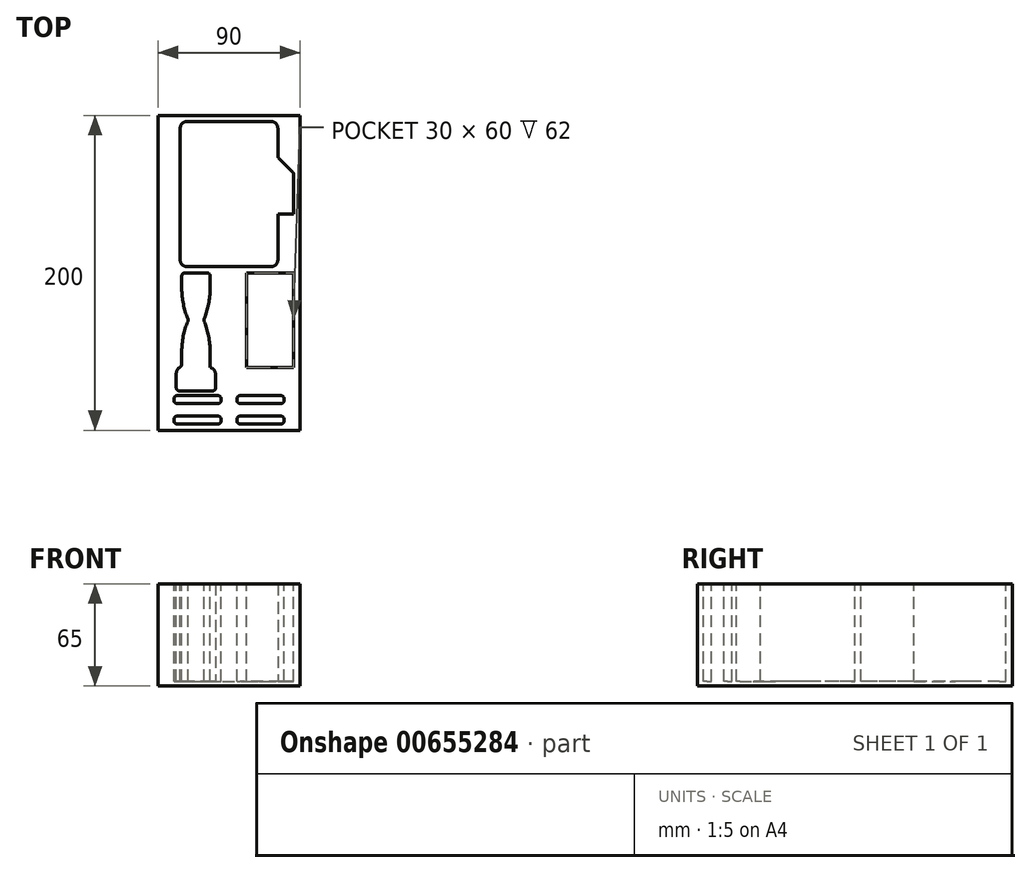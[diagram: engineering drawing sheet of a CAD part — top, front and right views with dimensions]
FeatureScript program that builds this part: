
annotation { "Feature Type Name" : "Feature", "Feature Type Description" : "" }
export const myFeature = defineFeature(function(context is Context, id is Id, definition is map)
    precondition{}
    {
        {
            var Q0;
            Q0=qCreatedBy(makeId("Top.planeOp"),FACE);
            var sketch = newSketch(context, id + "F0", { "sketchPlane" : qUnion([Q0])});
            skLineSegment(sketch, "E0.bottom", {"start": v(-45, -100) * mm, "end": v(45, -100) * mm});
            skLineSegment(sketch, "E0.top", {"start": v(-45, 100) * mm, "end": v(45, 100) * mm});
            skLineSegment(sketch, "E0.left", {"start": v(-45, -100) * mm, "end": v(-45, 100) * mm});
            skLineSegment(sketch, "E0.right", {"start": v(45, -100) * mm, "end": v(45, 100) * mm});
            skSolve(sketch);
        }
        {
            var Q0;
            Q0=makeQuery(id+"F0.imprint","IMPRINT",FACE,{"disambiguationData":[TD([[makeQuery(id+"F0.imprint","IMPRINT",EDGE,{"derivedFrom":sQuery(id+"F0.wireOp",EDGE,"E0.bottom")}),1.0]])]});
            extrude(context, id + "F1", {"entities" : qUnion([Q0]), "depth" : 65 * mm, "offsetDistance" : 25 * mm});
        }
        {
            var Q0;
            Q0=makeQuery(id+"F1.opExtrude","CAP_FACE",FACE,{"disambiguationData":[OSD([sQuery(id+"F0.wireOp",EDGE,"E0.bottom"),sQuery(id+"F0.wireOp",EDGE,"E0.top"),sQuery(id+"F0.wireOp",EDGE,"E0.left"),sQuery(id+"F0.wireOp",EDGE,"E0.right")])],"isStart":false});
            var sketch = newSketch(context, id + "F2", { "sketchPlane" : qUnion([Q0])});
            skLineSegment(sketch, "E1.bottom", {"start": v(-31, 96) * mm, "end": v(31, 96) * mm});
            skLineSegment(sketch, "E1.top", {"start": v(-31, 4) * mm, "end": v(31, 4) * mm});
            skLineSegment(sketch, "E1.left", {"start": v(-31, 96) * mm, "end": v(-31, 4) * mm});
            skLineSegment(sketch, "E1.right", {"start": v(31, 96) * mm, "end": v(31, 4) * mm});
            skLineSegment(sketch, "E2.bottom", {"start": v(-35, -96) * mm, "end": v(-5, -96) * mm});
            skLineSegment(sketch, "E2.top", {"start": v(-35, -91) * mm, "end": v(-5, -91) * mm});
            skLineSegment(sketch, "E2.left", {"start": v(-35, -96) * mm, "end": v(-35, -91) * mm});
            skLineSegment(sketch, "E2.right", {"start": v(-5, -96) * mm, "end": v(-5, -91) * mm});
            skLineSegment(sketch, "E3.bottom", {"start": v(-35, -83) * mm, "end": v(-5, -83) * mm});
            skLineSegment(sketch, "E3.top", {"start": v(-35, -78) * mm, "end": v(-5, -78) * mm});
            skLineSegment(sketch, "E3.left", {"start": v(-35, -83) * mm, "end": v(-35, -78) * mm});
            skLineSegment(sketch, "E3.right", {"start": v(-5, -83) * mm, "end": v(-5, -78) * mm});
            skLineSegment(sketch, "E4.bottom", {"start": v(11, 0) * mm, "end": v(41, 0) * mm});
            skLineSegment(sketch, "E4.top", {"start": v(11, -60) * mm, "end": v(41, -60) * mm});
            skLineSegment(sketch, "E4.left", {"start": v(11, 0) * mm, "end": v(11, -60) * mm});
            skLineSegment(sketch, "E4.right", {"start": v(41, 0) * mm, "end": v(41, -60) * mm});
            skLineSegment(sketch, "E5.MirrorCS", {"start": v(35, -96) * mm, "end": v(5, -96) * mm});
            skLineSegment(sketch, "E6.MirrorCS", {"start": v(35, -91) * mm, "end": v(5, -91) * mm});
            skLineSegment(sketch, "E7.MirrorCS", {"start": v(35, -78) * mm, "end": v(5, -78) * mm});
            skLineSegment(sketch, "E8.MirrorCS", {"start": v(5, -96) * mm, "end": v(5, -91) * mm});
            skLineSegment(sketch, "E9.MirrorCS", {"start": v(5, -83) * mm, "end": v(5, -78) * mm});
            skLineSegment(sketch, "E10.MirrorCS", {"start": v(35, -83) * mm, "end": v(5, -83) * mm});
            skLineSegment(sketch, "E11.MirrorCS", {"start": v(35, -83) * mm, "end": v(35, -78) * mm});
            skLineSegment(sketch, "E12.MirrorCS", {"start": v(35, -96) * mm, "end": v(35, -91) * mm});
            skLineSegment(sketch, "E13", {"start": v(-30, 0) * mm, "end": v(-12, 0) * mm});
            skLineSegment(sketch, "E14", {"start": v(-12, 0) * mm, "end": v(-12, -10) * mm});
            skLineSegment(sketch, "E15", {"start": v(-30, 0) * mm, "end": v(-30, -10) * mm});
            skArc(sketch, "E16", {"start": v(-30, -10) * mm, "mid": v(-28.95, -20.22) * mm, "end": v(-25.83, -30) * mm});
            skArc(sketch, "E17", {"start": v(-16.17, -30) * mm, "mid": v(-13.05, -20.22) * mm, "end": v(-12, -10) * mm});
            skLineSegment(sketch, "E18", {"start": v(-25.83, -30) * mm, "end": v(-16.17, -30) * mm, "construction": true});
            skLineSegment(sketch, "E19.MirrorCS", {"start": v(-30, -60) * mm, "end": v(-30, -50) * mm});
            skArc(sketch, "E20.MirrorCS", {"start": v(-30, -50) * mm, "mid": v(-28.95, -39.78) * mm, "end": v(-25.83, -30) * mm});
            skArc(sketch, "E21.MirrorCS", {"start": v(-16.17, -30) * mm, "mid": v(-13.05, -39.78) * mm, "end": v(-12, -50) * mm});
            skLineSegment(sketch, "E22.MirrorCS", {"start": v(-30, -60) * mm, "end": v(-12, -60) * mm});
            skLineSegment(sketch, "E23.MirrorCS", {"start": v(-12, -60) * mm, "end": v(-12, -50) * mm});
            skSolve(sketch);
        }
        {
            var Q0;
            Q0=makeQuery(id+"F2.imprint","IMPRINT",FACE,{"disambiguationData":[TD([[makeQuery(id+"F2.imprint","IMPRINT",EDGE,{"derivedFrom":sQuery(id+"F2.wireOp",EDGE,"E1.bottom")}),-1.0]])]});
            var Q1;
            Q1=makeQuery(id+"F2.imprint","IMPRINT",FACE,{"disambiguationData":[TD([[makeQuery(id+"F2.imprint","IMPRINT",EDGE,{"derivedFrom":sQuery(id+"F2.wireOp",EDGE,"E4.bottom")}),-1.0]])]});
            var Q2;
            Q2=makeQuery(id+"F2.imprint","IMPRINT",FACE,{"disambiguationData":[TD([[makeQuery(id+"F2.imprint","IMPRINT",EDGE,{"derivedFrom":sQuery(id+"F2.wireOp",EDGE,"E7.MirrorCS")}),1.0]])]});
            var Q3;
            Q3=makeQuery(id+"F2.imprint","IMPRINT",FACE,{"disambiguationData":[TD([[makeQuery(id+"F2.imprint","IMPRINT",EDGE,{"derivedFrom":sQuery(id+"F2.wireOp",EDGE,"E5.MirrorCS")}),-1.0]])]});
            var Q4;
            Q4=makeQuery(id+"F2.imprint","IMPRINT",FACE,{"disambiguationData":[TD([[makeQuery(id+"F2.imprint","IMPRINT",EDGE,{"derivedFrom":sQuery(id+"F2.wireOp",EDGE,"E2.bottom")}),1.0]])]});
            var Q5;
            Q5=makeQuery(id+"F2.imprint","IMPRINT",FACE,{"disambiguationData":[TD([[makeQuery(id+"F2.imprint","IMPRINT",EDGE,{"derivedFrom":sQuery(id+"F2.wireOp",EDGE,"E3.bottom")}),1.0]])]});
            var Q6;
            Q6=makeQuery(id+"F2.imprint","IMPRINT",FACE,{"disambiguationData":[TD([[makeQuery(id+"F2.imprint","IMPRINT",EDGE,{"derivedFrom":sQuery(id+"F2.wireOp",EDGE,"E13")}),-1.0]])]});
            extrude(context, id + "F3", {"entities" : qUnion([Q0, Q1, Q2, Q3, Q4, Q5, Q6]), "operationType" : NewBodyOperationType.REMOVE, "oppositeDirection" : true, "depth" : 62 * mm, "offsetDistance" : 25 * mm});
        }
        {
            var Q0;
            Q0=makeQuery(id+"F3.boolean.opBoolean","COPY",EDGE,{"derivedFrom":makeQuery(id+"F3.opExtrude","SWEPT_EDGE",EDGE,{"disambiguationData":[OSD([sQuery(id+"F2.wireOp",EDGE,"E1.bottom"),sQuery(id+"F2.wireOp",EDGE,"E1.left")])]})});
            var Q1;
            Q1=makeQuery(id+"F3.boolean.opBoolean","COPY",EDGE,{"derivedFrom":makeQuery(id+"F3.opExtrude","SWEPT_EDGE",EDGE,{"disambiguationData":[OSD([sQuery(id+"F2.wireOp",EDGE,"E1.bottom"),sQuery(id+"F2.wireOp",EDGE,"E1.right")])]})});
            var Q2;
            Q2=makeQuery(id+"F3.boolean.opBoolean","COPY",EDGE,{"derivedFrom":makeQuery(id+"F3.opExtrude","SWEPT_EDGE",EDGE,{"disambiguationData":[OSD([sQuery(id+"F2.wireOp",EDGE,"E1.top"),sQuery(id+"F2.wireOp",EDGE,"E1.left")])]})});
            var Q3;
            Q3=makeQuery(id+"F3.boolean.opBoolean","COPY",EDGE,{"derivedFrom":makeQuery(id+"F3.opExtrude","SWEPT_EDGE",EDGE,{"disambiguationData":[OSD([sQuery(id+"F2.wireOp",EDGE,"E1.top"),sQuery(id+"F2.wireOp",EDGE,"E1.right")])]})});
            fillet(context, id + "F4", {"entities" : qUnion([Q0, Q1, Q2, Q3]), "radius" : 4 * mm, "tangentPropagation" : true, "allowEdgeOverflow" : false});
        }
        {
            var Q0;
            Q0=makeQuery(id+"F3.boolean.opBoolean","COPY",FACE,{"derivedFrom":makeQuery(id+"F3.opExtrude","SWEPT_FACE",FACE,{"disambiguationData":[OSD([sQuery(id+"F2.wireOp",EDGE,"E1.bottom")])]})});
            var Q1;
            Q1=makeQuery(id+"F3.boolean.opBoolean","COPY",FACE,{"derivedFrom":makeQuery(id+"F3.opExtrude","SWEPT_FACE",FACE,{"disambiguationData":[OSD([sQuery(id+"F2.wireOp",EDGE,"E1.top")])]})});
            cPlane(context, id + "F5", {"entities" : qUnion([Q0, Q1]), "cplaneType" : CPlaneType.MID_PLANE, "offset" : 25 * mm, "width" : 150 * mm, "height" : 150 * mm});
        }
        {
            var Q0;
            Q0=makeQuery(id+"F1.opExtrude","CAP_FACE",FACE,{"disambiguationData":[OSD([sQuery(id+"F0.wireOp",EDGE,"E0.bottom"),sQuery(id+"F0.wireOp",EDGE,"E0.top"),sQuery(id+"F0.wireOp",EDGE,"E0.left"),sQuery(id+"F0.wireOp",EDGE,"E0.right")])],"isStart":false});
            var sketch = newSketch(context, id + "F6", { "sketchPlane" : qUnion([Q0])});
            skLineSegment(sketch, "E24.bottom", {"start": v(31, 62.5) * mm, "end": v(41, 62.5) * mm});
            skLineSegment(sketch, "E24.top", {"start": v(31, 37.5) * mm, "end": v(41, 37.5) * mm});
            skLineSegment(sketch, "E24.left", {"start": v(31, 62.5) * mm, "end": v(31, 37.5) * mm});
            skLineSegment(sketch, "E24.right", {"start": v(41, 62.5) * mm, "end": v(41, 37.5) * mm});
            skLineSegment(sketch, "E25.bottom", {"start": v(-33.5, -60) * mm, "end": v(-8.5, -60) * mm});
            skLineSegment(sketch, "E25.top", {"start": v(-33.5, -75) * mm, "end": v(-8.5, -75) * mm});
            skLineSegment(sketch, "E25.left", {"start": v(-33.5, -60) * mm, "end": v(-33.5, -75) * mm});
            skLineSegment(sketch, "E25.right", {"start": v(-8.5, -60) * mm, "end": v(-8.5, -75) * mm});
            skLineSegment(sketch, "E26", {"start": v(-21, 0) * mm, "end": v(-21, -60) * mm, "construction": true});
            skSolve(sketch);
        }
        {
            var Q0;
            Q0=makeQuery(id+"F6.imprint","IMPRINT",FACE,{"disambiguationData":[TD([[makeQuery(id+"F6.imprint","IMPRINT",EDGE,{"derivedFrom":sQuery(id+"F6.wireOp",EDGE,"E24.bottom")}),-1.0]])]});
            var Q1;
            Q1=makeQuery(id+"F6.imprint","IMPRINT",FACE,{"disambiguationData":[TD([[makeQuery(id+"F6.imprint","IMPRINT",EDGE,{"derivedFrom":sQuery(id+"F6.wireOp",EDGE,"E25.top")}),1.0]])]});
            var Q2;
            Q2=makeQuery(id+"F3.boolean.opBoolean","COPY",FACE,{"derivedFrom":makeQuery(id+"F3.opExtrude","CAP_FACE",FACE,{"disambiguationData":[OSD([sQuery(id+"F2.wireOp",EDGE,"E1.bottom"),sQuery(id+"F2.wireOp",EDGE,"E1.top"),sQuery(id+"F2.wireOp",EDGE,"E1.left"),sQuery(id+"F2.wireOp",EDGE,"E1.right")])],"isStart":false})});
            extrude(context, id + "F7", {"entities" : qUnion([Q0, Q1]), "operationType" : NewBodyOperationType.REMOVE, "endBound" : BoundingType.UP_TO_SURFACE, "oppositeDirection" : true, "depth" : 25 * mm, "endBoundEntityFace" : qUnion([Q2]), "offsetDistance" : 25 * mm});
        }
        {
            var Q0;
            Q0=makeQuery(id+"F7.boolean.opBoolean","COPY",EDGE,{"derivedFrom":makeQuery(id+"F7.opExtrude","SWEPT_EDGE",EDGE,{"disambiguationData":[OSD([sQuery(id+"F2.wireOp",EDGE,"E1.right"),sQuery(id+"F6.wireOp",EDGE,"E24.bottom"),sQuery(id+"F6.wireOp",EDGE,"E24.left")])]})});
            var Q1;
            Q1=makeQuery(id+"F7.boolean.opBoolean","COPY",EDGE,{"derivedFrom":makeQuery(id+"F7.opExtrude","SWEPT_EDGE",EDGE,{"disambiguationData":[OSD([sQuery(id+"F2.wireOp",EDGE,"E1.right"),sQuery(id+"F6.wireOp",EDGE,"E24.top"),sQuery(id+"F6.wireOp",EDGE,"E24.left")])]})});
            chamfer(context, id + "F8", {"entities" : qUnion([Q0, Q1]), "width" : 11 * mm, "tangentPropagation" : true});
        }
        {
            var Q0;
            {var subQ0=sQuery(id+"F2.wireOp",EDGE,"E1.right");var subQ4=sQuery(id+"F6.wireOp",EDGE,"E24.bottom");Q0=makeQuery(id+"F8.opChamfer","BLEND_EDGE",EDGE,{"blendedFrom":[makeQuery(id+"F7.boolean.opBoolean","COPY",EDGE,{"derivedFrom":makeQuery(id+"F7.opExtrude","SWEPT_EDGE",EDGE,{"disambiguationData":[OSD([subQ0,subQ4,sQuery(id+"F6.wireOp",EDGE,"E24.left")])]})}),makeQuery(id+"F7.boolean.opBoolean","SPLIT",FACE,{"disambiguationData":[TD([makeQuery(id+"F7.opExtrude","SWEPT_FACE",FACE,{"disambiguationData":[OSD([subQ4])]})])],"derivedFrom":makeQuery(id+"F3.boolean.opBoolean","COPY",FACE,{"derivedFrom":makeQuery(id+"F3.opExtrude","SWEPT_FACE",FACE,{"disambiguationData":[OSD([subQ0])]})})})],"blendedInto":[makeQuery(id+"F7.boolean.opBoolean","SPLIT",FACE,{"disambiguationData":[TD([makeQuery(id+"F7.opExtrude","SWEPT_FACE",FACE,{"disambiguationData":[OSD([subQ4])]})])],"derivedFrom":makeQuery(id+"F3.boolean.opBoolean","COPY",FACE,{"derivedFrom":makeQuery(id+"F3.opExtrude","SWEPT_FACE",FACE,{"disambiguationData":[OSD([subQ0])]})})})]});}
            var Q1;
            Q1=makeQuery(id+"F8.opChamfer","BLEND_EDGE",EDGE,{"blendedFrom":[makeQuery(id+"F7.boolean.opBoolean","COPY",EDGE,{"derivedFrom":makeQuery(id+"F7.opExtrude","SWEPT_EDGE",EDGE,{"disambiguationData":[OSD([sQuery(id+"F2.wireOp",EDGE,"E1.right"),sQuery(id+"F6.wireOp",EDGE,"E24.bottom"),sQuery(id+"F6.wireOp",EDGE,"E24.left")])]})}),makeQuery(id+"F7.boolean.opBoolean","COPY",FACE,{"derivedFrom":makeQuery(id+"F7.opExtrude","SWEPT_FACE",FACE,{"disambiguationData":[OSD([sQuery(id+"F6.wireOp",EDGE,"E24.right")])]})})],"blendedInto":[makeQuery(id+"F7.boolean.opBoolean","COPY",FACE,{"derivedFrom":makeQuery(id+"F7.opExtrude","SWEPT_FACE",FACE,{"disambiguationData":[OSD([sQuery(id+"F6.wireOp",EDGE,"E24.right")])]})})]});
            var Q2;
            Q2=makeQuery(id+"F8.opChamfer","BLEND_EDGE",EDGE,{"blendedFrom":[makeQuery(id+"F7.boolean.opBoolean","COPY",EDGE,{"derivedFrom":makeQuery(id+"F7.opExtrude","SWEPT_EDGE",EDGE,{"disambiguationData":[OSD([sQuery(id+"F2.wireOp",EDGE,"E1.right"),sQuery(id+"F6.wireOp",EDGE,"E24.top"),sQuery(id+"F6.wireOp",EDGE,"E24.left")])]})}),makeQuery(id+"F7.boolean.opBoolean","COPY",FACE,{"derivedFrom":makeQuery(id+"F7.opExtrude","SWEPT_FACE",FACE,{"disambiguationData":[OSD([sQuery(id+"F6.wireOp",EDGE,"E24.right")])]})})],"blendedInto":[makeQuery(id+"F7.boolean.opBoolean","COPY",FACE,{"derivedFrom":makeQuery(id+"F7.opExtrude","SWEPT_FACE",FACE,{"disambiguationData":[OSD([sQuery(id+"F6.wireOp",EDGE,"E24.right")])]})})]});
            var Q3;
            {var subQ0=sQuery(id+"F2.wireOp",EDGE,"E1.right");var subQ4=sQuery(id+"F6.wireOp",EDGE,"E24.top");Q3=makeQuery(id+"F8.opChamfer","BLEND_EDGE",EDGE,{"blendedFrom":[makeQuery(id+"F7.boolean.opBoolean","COPY",EDGE,{"derivedFrom":makeQuery(id+"F7.opExtrude","SWEPT_EDGE",EDGE,{"disambiguationData":[OSD([subQ0,subQ4,sQuery(id+"F6.wireOp",EDGE,"E24.left")])]})}),makeQuery(id+"F7.boolean.opBoolean","SPLIT",FACE,{"disambiguationData":[TD([makeQuery(id+"F7.opExtrude","SWEPT_FACE",FACE,{"disambiguationData":[OSD([subQ4])]})])],"derivedFrom":makeQuery(id+"F3.boolean.opBoolean","COPY",FACE,{"derivedFrom":makeQuery(id+"F3.opExtrude","SWEPT_FACE",FACE,{"disambiguationData":[OSD([subQ0])]})})})],"blendedInto":[makeQuery(id+"F7.boolean.opBoolean","SPLIT",FACE,{"disambiguationData":[TD([makeQuery(id+"F7.opExtrude","SWEPT_FACE",FACE,{"disambiguationData":[OSD([subQ4])]})])],"derivedFrom":makeQuery(id+"F3.boolean.opBoolean","COPY",FACE,{"derivedFrom":makeQuery(id+"F3.opExtrude","SWEPT_FACE",FACE,{"disambiguationData":[OSD([subQ0])]})})})]});}
            var Q4;
            Q4=makeQuery(id+"F3.boolean.opBoolean","COPY",EDGE,{"derivedFrom":makeQuery(id+"F3.opExtrude","SWEPT_EDGE",EDGE,{"disambiguationData":[OSD([sQuery(id+"F2.wireOp",EDGE,"E13"),sQuery(id+"F2.wireOp",EDGE,"E15")])]})});
            var Q5;
            Q5=makeQuery(id+"F3.boolean.opBoolean","COPY",EDGE,{"derivedFrom":makeQuery(id+"F3.opExtrude","SWEPT_EDGE",EDGE,{"disambiguationData":[OSD([sQuery(id+"F2.wireOp",EDGE,"E13"),sQuery(id+"F2.wireOp",EDGE,"E14")])]})});
            var Q6;
            Q6=makeQuery(id+"F3.boolean.opBoolean","COPY",EDGE,{"derivedFrom":makeQuery(id+"F3.opExtrude","SWEPT_EDGE",EDGE,{"disambiguationData":[OSD([sQuery(id+"F2.wireOp",EDGE,"E17"),sQuery(id+"F2.wireOp",EDGE,"E21.MirrorCS")])]})});
            var Q7;
            Q7=makeQuery(id+"F3.boolean.opBoolean","COPY",EDGE,{"derivedFrom":makeQuery(id+"F3.opExtrude","SWEPT_EDGE",EDGE,{"disambiguationData":[OSD([sQuery(id+"F2.wireOp",EDGE,"E16"),sQuery(id+"F2.wireOp",EDGE,"E20.MirrorCS")])]})});
            var Q8;
            Q8=makeQuery(id+"F3.boolean.opBoolean","COPY",EDGE,{"derivedFrom":makeQuery(id+"F3.opExtrude","SWEPT_EDGE",EDGE,{"disambiguationData":[OSD([sQuery(id+"F2.wireOp",EDGE,"E19.MirrorCS"),sQuery(id+"F2.wireOp",EDGE,"E22.MirrorCS")])]})});
            var Q9;
            Q9=makeQuery(id+"F3.boolean.opBoolean","COPY",EDGE,{"derivedFrom":makeQuery(id+"F3.opExtrude","SWEPT_EDGE",EDGE,{"disambiguationData":[OSD([sQuery(id+"F2.wireOp",EDGE,"E22.MirrorCS"),sQuery(id+"F2.wireOp",EDGE,"E23.MirrorCS")])]})});
            var Q10;
            Q10=makeQuery(id+"F7.boolean.opBoolean","COPY",EDGE,{"derivedFrom":makeQuery(id+"F7.opExtrude","SWEPT_EDGE",EDGE,{"disambiguationData":[OSD([sQuery(id+"F6.wireOp",EDGE,"E25.top"),sQuery(id+"F6.wireOp",EDGE,"E25.right")])]})});
            var Q11;
            Q11=makeQuery(id+"F7.boolean.opBoolean","COPY",EDGE,{"derivedFrom":makeQuery(id+"F7.opExtrude","SWEPT_EDGE",EDGE,{"disambiguationData":[OSD([sQuery(id+"F6.wireOp",EDGE,"E25.top"),sQuery(id+"F6.wireOp",EDGE,"E25.left")])]})});
            var Q12;
            Q12=makeQuery(id+"F3.boolean.opBoolean","COPY",EDGE,{"derivedFrom":makeQuery(id+"F3.opExtrude","SWEPT_EDGE",EDGE,{"disambiguationData":[OSD([sQuery(id+"F2.wireOp",EDGE,"E3.top"),sQuery(id+"F2.wireOp",EDGE,"E3.left")])]})});
            var Q13;
            Q13=makeQuery(id+"F3.boolean.opBoolean","COPY",EDGE,{"derivedFrom":makeQuery(id+"F3.opExtrude","SWEPT_EDGE",EDGE,{"disambiguationData":[OSD([sQuery(id+"F2.wireOp",EDGE,"E2.top"),sQuery(id+"F2.wireOp",EDGE,"E2.left")])]})});
            var Q14;
            Q14=makeQuery(id+"F3.boolean.opBoolean","COPY",EDGE,{"derivedFrom":makeQuery(id+"F3.opExtrude","SWEPT_EDGE",EDGE,{"disambiguationData":[OSD([sQuery(id+"F2.wireOp",EDGE,"E6.MirrorCS"),sQuery(id+"F2.wireOp",EDGE,"E8.MirrorCS")])]})});
            var Q15;
            Q15=makeQuery(id+"F3.boolean.opBoolean","COPY",EDGE,{"derivedFrom":makeQuery(id+"F3.opExtrude","SWEPT_EDGE",EDGE,{"disambiguationData":[OSD([sQuery(id+"F2.wireOp",EDGE,"E7.MirrorCS"),sQuery(id+"F2.wireOp",EDGE,"E9.MirrorCS")])]})});
            var Q16;
            Q16=makeQuery(id+"F3.boolean.opBoolean","COPY",EDGE,{"derivedFrom":makeQuery(id+"F3.opExtrude","SWEPT_EDGE",EDGE,{"disambiguationData":[OSD([sQuery(id+"F2.wireOp",EDGE,"E2.top"),sQuery(id+"F2.wireOp",EDGE,"E2.right")])]})});
            var Q17;
            Q17=makeQuery(id+"F3.boolean.opBoolean","COPY",EDGE,{"derivedFrom":makeQuery(id+"F3.opExtrude","SWEPT_EDGE",EDGE,{"disambiguationData":[OSD([sQuery(id+"F2.wireOp",EDGE,"E3.top"),sQuery(id+"F2.wireOp",EDGE,"E3.right")])]})});
            var Q18;
            Q18=makeQuery(id+"F3.boolean.opBoolean","COPY",EDGE,{"derivedFrom":makeQuery(id+"F3.opExtrude","SWEPT_EDGE",EDGE,{"disambiguationData":[OSD([sQuery(id+"F2.wireOp",EDGE,"E7.MirrorCS"),sQuery(id+"F2.wireOp",EDGE,"E11.MirrorCS")])]})});
            var Q19;
            Q19=makeQuery(id+"F3.boolean.opBoolean","COPY",EDGE,{"derivedFrom":makeQuery(id+"F3.opExtrude","SWEPT_EDGE",EDGE,{"disambiguationData":[OSD([sQuery(id+"F2.wireOp",EDGE,"E6.MirrorCS"),sQuery(id+"F2.wireOp",EDGE,"E12.MirrorCS")])]})});
            var Q20;
            Q20=makeQuery(id+"F3.boolean.opBoolean","COPY",EDGE,{"derivedFrom":makeQuery(id+"F3.opExtrude","SWEPT_EDGE",EDGE,{"disambiguationData":[OSD([sQuery(id+"F2.wireOp",EDGE,"E3.bottom"),sQuery(id+"F2.wireOp",EDGE,"E3.right")])]})});
            var Q21;
            Q21=makeQuery(id+"F3.boolean.opBoolean","COPY",EDGE,{"derivedFrom":makeQuery(id+"F3.opExtrude","SWEPT_EDGE",EDGE,{"disambiguationData":[OSD([sQuery(id+"F2.wireOp",EDGE,"E2.bottom"),sQuery(id+"F2.wireOp",EDGE,"E2.right")])]})});
            var Q22;
            Q22=makeQuery(id+"F3.boolean.opBoolean","COPY",EDGE,{"derivedFrom":makeQuery(id+"F3.opExtrude","SWEPT_EDGE",EDGE,{"disambiguationData":[OSD([sQuery(id+"F2.wireOp",EDGE,"E5.MirrorCS"),sQuery(id+"F2.wireOp",EDGE,"E12.MirrorCS")])]})});
            var Q23;
            Q23=makeQuery(id+"F3.boolean.opBoolean","COPY",EDGE,{"derivedFrom":makeQuery(id+"F3.opExtrude","SWEPT_EDGE",EDGE,{"disambiguationData":[OSD([sQuery(id+"F2.wireOp",EDGE,"E10.MirrorCS"),sQuery(id+"F2.wireOp",EDGE,"E11.MirrorCS")])]})});
            var Q24;
            Q24=makeQuery(id+"F3.boolean.opBoolean","COPY",EDGE,{"derivedFrom":makeQuery(id+"F3.opExtrude","SWEPT_EDGE",EDGE,{"disambiguationData":[OSD([sQuery(id+"F2.wireOp",EDGE,"E5.MirrorCS"),sQuery(id+"F2.wireOp",EDGE,"E8.MirrorCS")])]})});
            var Q25;
            Q25=makeQuery(id+"F3.boolean.opBoolean","COPY",EDGE,{"derivedFrom":makeQuery(id+"F3.opExtrude","SWEPT_EDGE",EDGE,{"disambiguationData":[OSD([sQuery(id+"F2.wireOp",EDGE,"E9.MirrorCS"),sQuery(id+"F2.wireOp",EDGE,"E10.MirrorCS")])]})});
            var Q26;
            Q26=makeQuery(id+"F3.boolean.opBoolean","COPY",EDGE,{"derivedFrom":makeQuery(id+"F3.opExtrude","SWEPT_EDGE",EDGE,{"disambiguationData":[OSD([sQuery(id+"F2.wireOp",EDGE,"E3.bottom"),sQuery(id+"F2.wireOp",EDGE,"E3.left")])]})});
            var Q27;
            Q27=makeQuery(id+"F3.boolean.opBoolean","COPY",EDGE,{"derivedFrom":makeQuery(id+"F3.opExtrude","SWEPT_EDGE",EDGE,{"disambiguationData":[OSD([sQuery(id+"F2.wireOp",EDGE,"E2.bottom"),sQuery(id+"F2.wireOp",EDGE,"E2.left")])]})});
            fillet(context, id + "F9", {"entities" : qUnion([Q0, Q1, Q2, Q3, Q4, Q5, Q6, Q7, Q8, Q9, Q10, Q11, Q12, Q13, Q14, Q15, Q16, Q17, Q18, Q19, Q20, Q21, Q22, Q23, Q24, Q25, Q26, Q27]), "radius" : 2 * mm, "tangentPropagation" : true, "allowEdgeOverflow" : false});
        }
        {
            var Q0;
            Q0=makeQuery(id+"F7.boolean.opBoolean","COPY",EDGE,{"derivedFrom":makeQuery(id+"F7.opExtrude","SWEPT_EDGE",EDGE,{"disambiguationData":[OSD([sQuery(id+"F6.wireOp",EDGE,"E25.bottom"),sQuery(id+"F6.wireOp",EDGE,"E25.left")])]})});
            var Q1;
            Q1=makeQuery(id+"F7.boolean.opBoolean","COPY",EDGE,{"derivedFrom":makeQuery(id+"F7.opExtrude","SWEPT_EDGE",EDGE,{"disambiguationData":[OSD([sQuery(id+"F6.wireOp",EDGE,"E25.bottom"),sQuery(id+"F6.wireOp",EDGE,"E25.right")])]})});
            fillet(context, id + "F10", {"entities" : qUnion([Q0, Q1]), "radius" : 5 * mm, "tangentPropagation" : true, "allowEdgeOverflow" : false});
        }
    });
